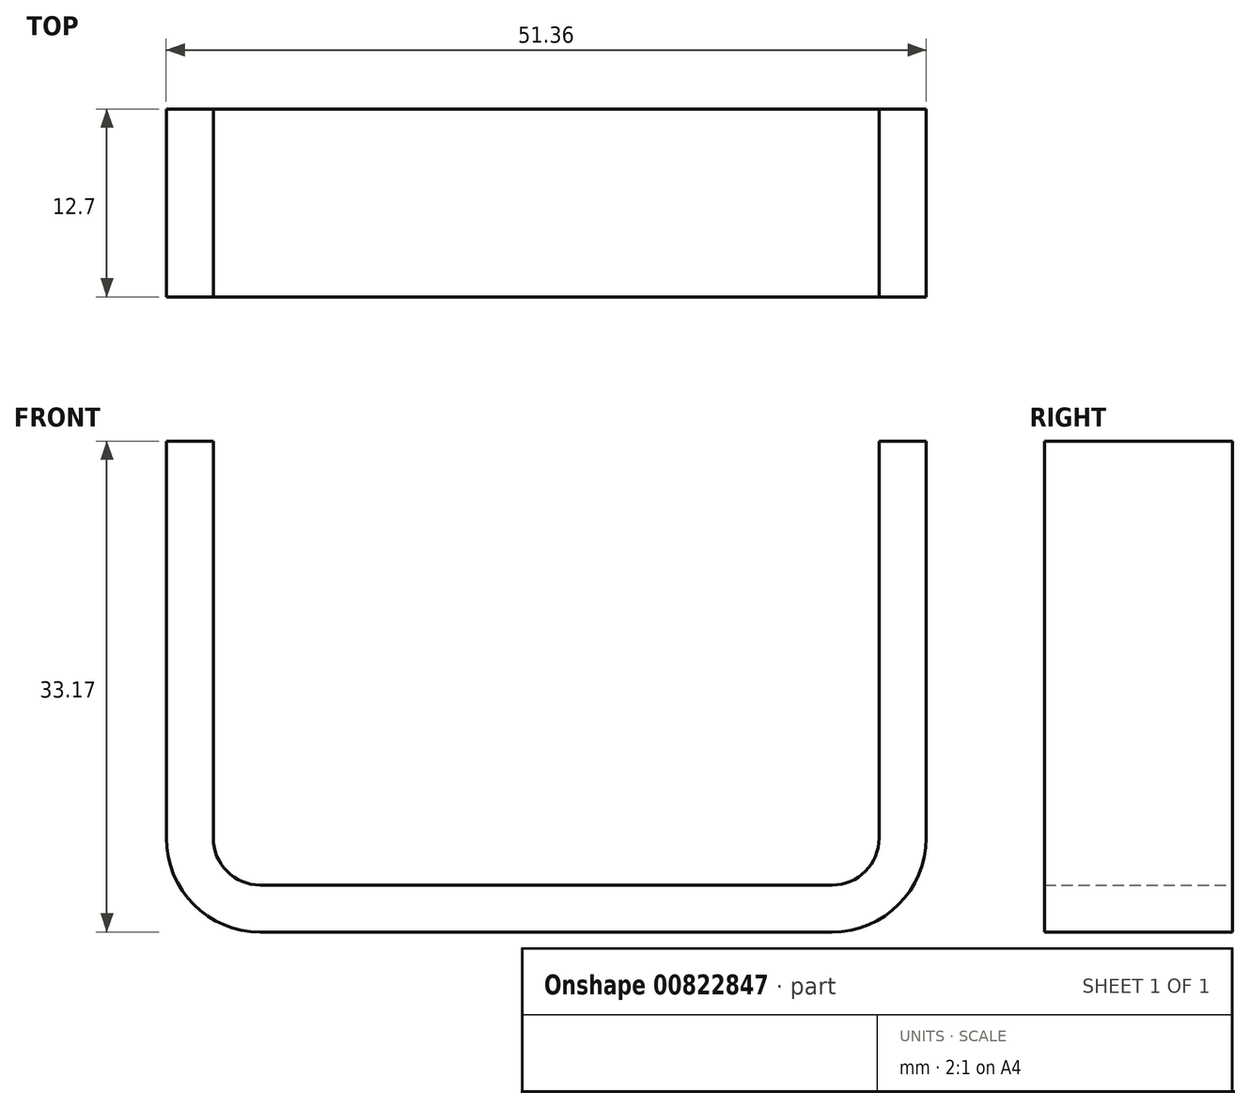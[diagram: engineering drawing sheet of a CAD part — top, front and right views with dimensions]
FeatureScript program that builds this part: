
annotation { "Feature Type Name" : "Feature", "Feature Type Description" : "" }
export const myFeature = defineFeature(function(context is Context, id is Id, definition is map)
    precondition{}
    {
        {
            var Q0;
            Q0=qCreatedBy(makeId("Front.planeOp"),FACE);
            var sketch = newSketch(context, id + "F0", { "sketchPlane" : qUnion([Q0])});
            skLineSegment(sketch, "E0", {"start": v(0, 0) * mm, "end": v(0, 17.47) * mm, "construction": true});
            skLineSegment(sketch, "E1", {"start": v(0, 0) * mm, "end": v(-22.5, 0) * mm});
            skLineSegment(sketch, "E2", {"start": v(-22.5, 0) * mm, "end": v(-22.5, 30) * mm});
            skLineSegment(sketch, "E3.MirrorCS", {"start": v(0, 0) * mm, "end": v(22.5, 0) * mm});
            skLineSegment(sketch, "E4.MirrorCS", {"start": v(22.5, 0) * mm, "end": v(22.5, 30) * mm});
            skLineSegment(sketch, "E5.0", {"start": v(-25.68, -3.18) * mm, "end": v(-25.68, 30) * mm});
            skLineSegment(sketch, "E5.1", {"start": v(0, -3.17) * mm, "end": v(-25.68, -3.18) * mm});
            skLineSegment(sketch, "E5.2", {"start": v(0, -3.17) * mm, "end": v(25.68, -3.17) * mm});
            skLineSegment(sketch, "E5.3", {"start": v(25.68, -3.18) * mm, "end": v(25.68, 30) * mm});
            skLineSegment(sketch, "E6", {"start": v(-25.68, 30) * mm, "end": v(-22.5, 30) * mm});
            skLineSegment(sketch, "E7", {"start": v(22.5, 30) * mm, "end": v(25.68, 30) * mm});
            skSolve(sketch);
        }
        {
            var Q0;
            Q0=qSketchRegion(id+"F0",true);
            extrude(context, id + "F1", {"entities" : qUnion([Q0]), "endBound" : BoundingType.SYMMETRIC, "depth" : 12.7 * mm, "offsetDistance" : 25 * mm});
        }
        {
            var Q0;
            Q0=makeQuery(id+"F1.opExtrude","SWEPT_EDGE",EDGE,{"disambiguationData":[OSD([sQuery(id+"F0.wireOp",EDGE,"E3.MirrorCS"),sQuery(id+"F0.wireOp",EDGE,"E4.MirrorCS")])]});
            var Q1;
            Q1=makeQuery(id+"F1.opExtrude","SWEPT_EDGE",EDGE,{"disambiguationData":[OSD([sQuery(id+"F0.wireOp",EDGE,"E1"),sQuery(id+"F0.wireOp",EDGE,"E2")])]});
            fillet(context, id + "F2", {"entities" : qUnion([Q0, Q1]), "radius" : (25.4 / 8) * mm, "tangentPropagation" : true, "allowEdgeOverflow" : false});
        }
        {
            var Q0;
            Q0=makeQuery(id+"F1.opExtrude","SWEPT_EDGE",EDGE,{"disambiguationData":[OSD([sQuery(id+"F0.wireOp",EDGE,"E5.0"),sQuery(id+"F0.wireOp",EDGE,"E5.1")])]});
            var Q1;
            Q1=makeQuery(id+"F1.opExtrude","SWEPT_EDGE",EDGE,{"disambiguationData":[OSD([sQuery(id+"F0.wireOp",EDGE,"E5.2"),sQuery(id+"F0.wireOp",EDGE,"E5.3")])]});
            fillet(context, id + "F3", {"entities" : qUnion([Q0, Q1]), "radius" : ((25.4 / 8) * 2) * mm, "tangentPropagation" : true, "allowEdgeOverflow" : false});
        }
    });
